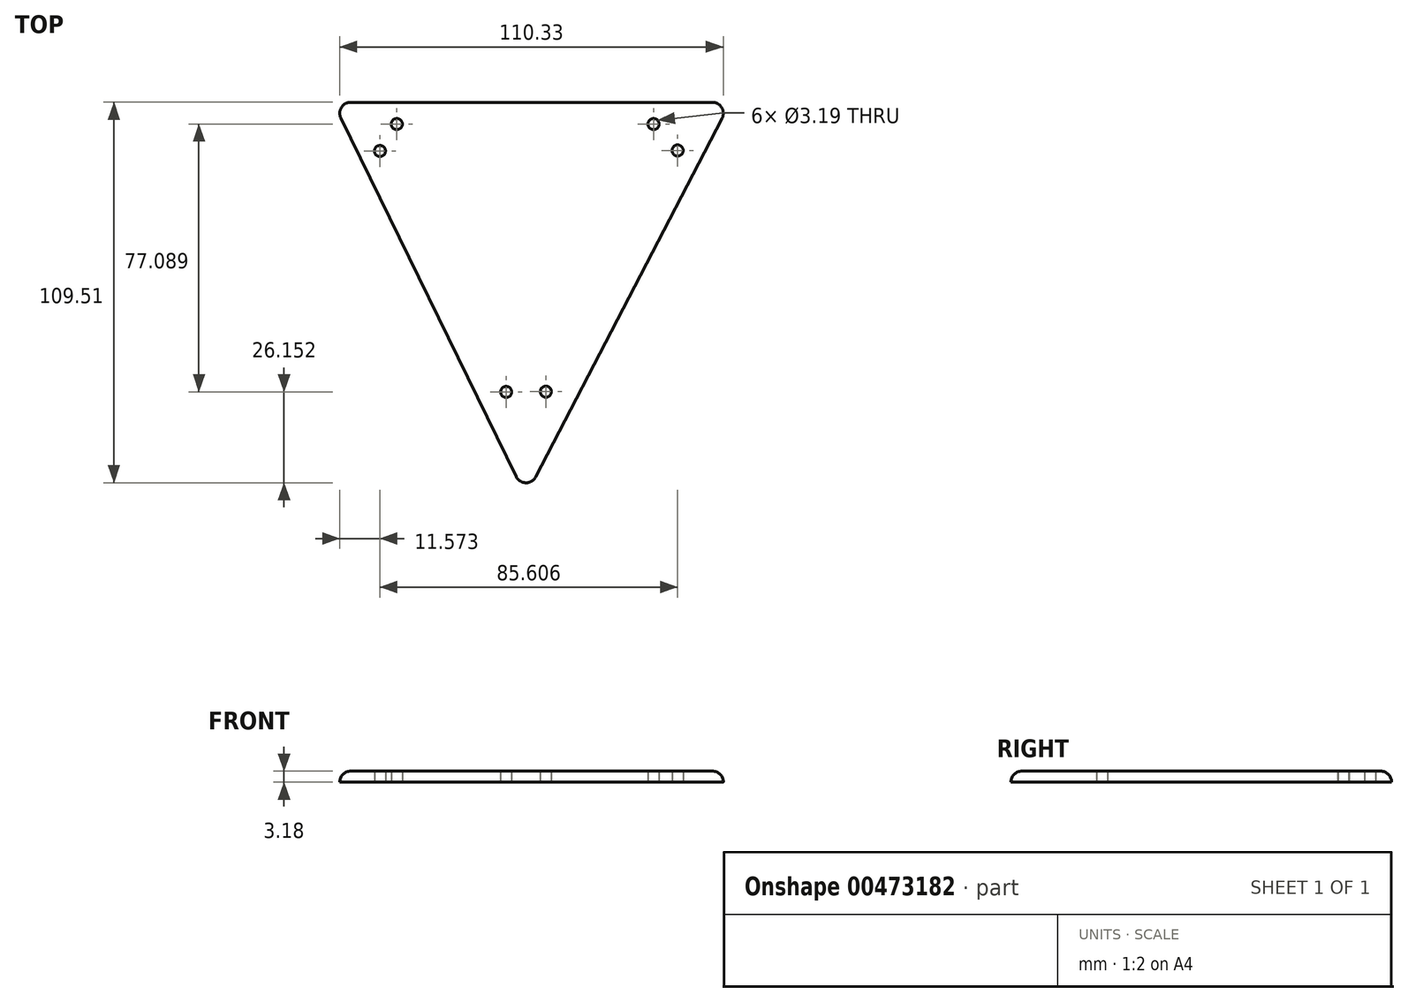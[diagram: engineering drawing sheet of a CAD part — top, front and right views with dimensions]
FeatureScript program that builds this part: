
annotation { "Feature Type Name" : "Feature", "Feature Type Description" : "" }
export const myFeature = defineFeature(function(context is Context, id is Id, definition is map)
    precondition{}
    {
        {
            var Q0;
            Q0=qCreatedBy(makeId("Top.planeOp"),FACE);
            var sketch = newSketch(context, id + "F0", { "sketchPlane" : qUnion([Q0])});
            skLineSegment(sketch, "E0", {"start": v(-55.4, 56.2) * mm, "end": v(58.89, 56.2) * mm});
            skLineSegment(sketch, "E1", {"start": v(58.89, 56.2) * mm, "end": v(0, -57.18) * mm});
            skLineSegment(sketch, "E2", {"start": v(0, -57.18) * mm, "end": v(-55.4, 56.2) * mm});
            skCircle(sketch, "E3", {"center": v(-41.93, 42.2) * mm, "radius": 1.6 * mm});
            skCircle(sketch, "E4", {"center": v(-37.09, 49.94) * mm, "radius": 1.6 * mm});
            skCircle(sketch, "E5", {"center": v(36.76, 49.94) * mm, "radius": 1.6 * mm});
            skCircle(sketch, "E6", {"center": v(43.68, 42.33) * mm, "radius": 1.6 * mm});
            skCircle(sketch, "E7", {"center": v(-5.64, -27.15) * mm, "radius": 1.6 * mm});
            skCircle(sketch, "E8", {"center": v(5.79, -27.1) * mm, "radius": 1.6 * mm});
            skSolve(sketch);
        }
        {
            var Q0;
            Q0=makeQuery(id+"F0.imprint","IMPRINT",FACE,{"disambiguationData":[TD([[makeQuery(id+"F0.imprint","IMPRINT",EDGE,{"derivedFrom":sQuery(id+"F0.wireOp",EDGE,"E0")}),-1.0]])]});
            extrude(context, id + "F1", {"entities" : qUnion([Q0]), "depth" : 3.17 * mm});
        }
        {
            var Q0;
            Q0=makeQuery(id+"F1.opExtrude","CAP_EDGE",EDGE,{"disambiguationData":[OSD([sQuery(id+"F0.wireOp",EDGE,"E2")])],"isStart":false});
            var Q1;
            Q1=makeQuery(id+"F1.opExtrude","CAP_EDGE",EDGE,{"disambiguationData":[OSD([sQuery(id+"F0.wireOp",EDGE,"E1")])],"isStart":false});
            var Q2;
            Q2=makeQuery(id+"F1.opExtrude","CAP_EDGE",EDGE,{"disambiguationData":[OSD([sQuery(id+"F0.wireOp",EDGE,"E0")])],"isStart":false});
            var Q3;
            Q3=makeQuery(id+"F1.opExtrude","SWEPT_EDGE",EDGE,{"disambiguationData":[OSD([sQuery(id+"F0.wireOp",EDGE,"E1"),sQuery(id+"F0.wireOp",EDGE,"E2")])]});
            var Q4;
            Q4=makeQuery(id+"F1.opExtrude","SWEPT_EDGE",EDGE,{"disambiguationData":[OSD([sQuery(id+"F0.wireOp",EDGE,"E0"),sQuery(id+"F0.wireOp",EDGE,"E2")])]});
            var Q5;
            Q5=makeQuery(id+"F1.opExtrude","SWEPT_EDGE",EDGE,{"disambiguationData":[OSD([sQuery(id+"F0.wireOp",EDGE,"E0"),sQuery(id+"F0.wireOp",EDGE,"E1")])]});
            fillet(context, id + "F2", {"entities" : qUnion([Q0, Q1, Q2, Q3, Q4, Q5]), "radius" : 3.17 * mm, "tangentPropagation" : true, "allowEdgeOverflow" : false});
        }
    });
